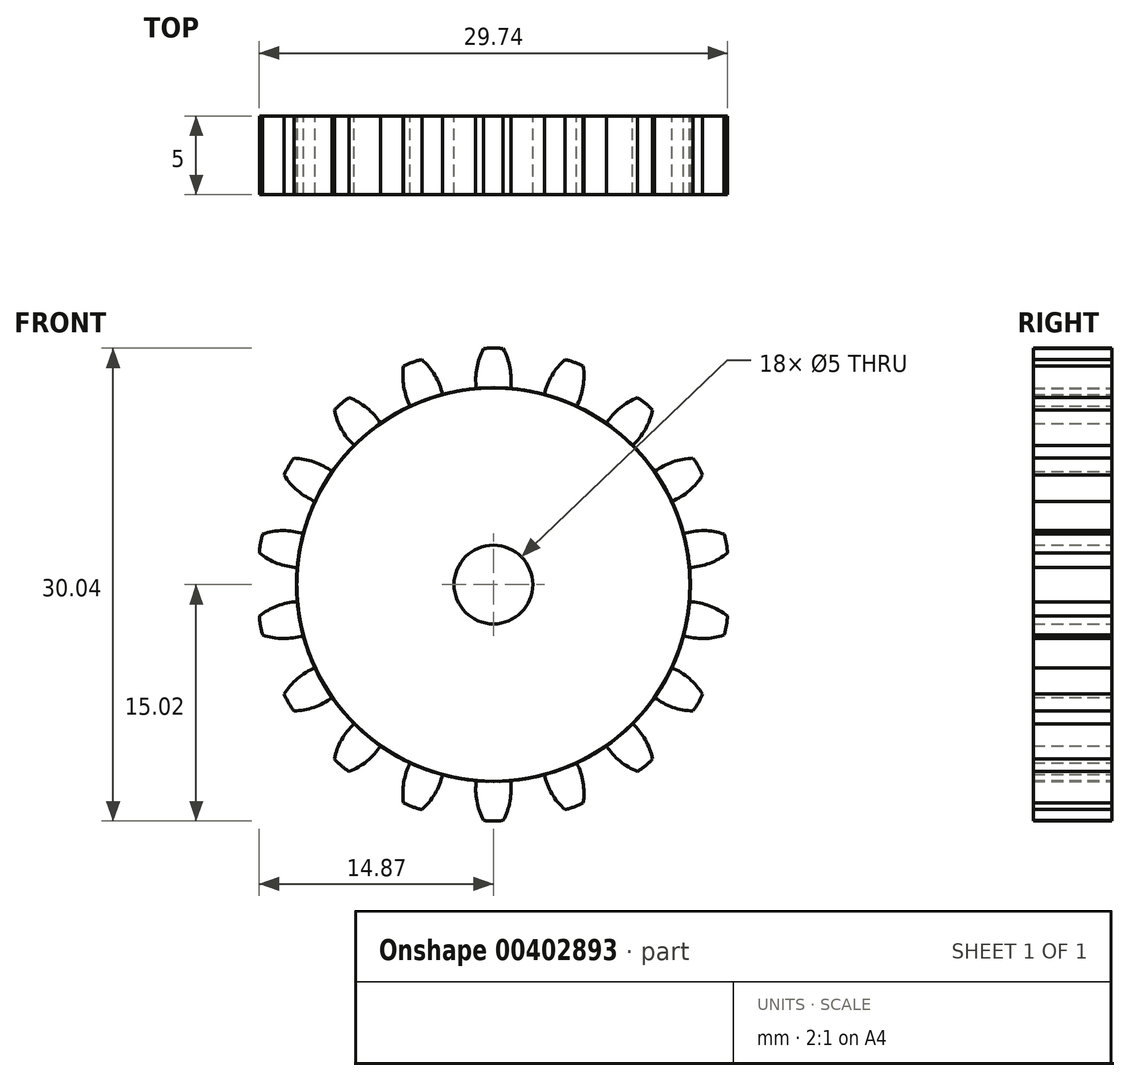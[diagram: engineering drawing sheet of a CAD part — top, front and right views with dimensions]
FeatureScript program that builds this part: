
annotation { "Feature Type Name" : "Feature", "Feature Type Description" : "" }
export const myFeature = defineFeature(function(context is Context, id is Id, definition is map)
    precondition{}
    {
        {
            var Q0;
            Q0=qCreatedBy(makeId("Front.planeOp"),FACE);
            var sketch = newSketch(context, id + "F0", { "sketchPlane" : qUnion([Q0])});
            skCircle(sketch, "E0", {"center": v(0, 0) * mm, "radius": 12.5 * mm});
            skArc(sketch, "E1", {"start": v(-0.61, 14.99) * mm, "mid": v(-1.05, 13.76) * mm, "end": v(-1.09, 12.45) * mm});
            skArc(sketch, "E2.MirrorCS", {"start": v(0.61, 14.99) * mm, "mid": v(1.05, 13.76) * mm, "end": v(1.09, 12.45) * mm});
            skArc(sketch, "E3", {"start": v(0.61, 14.99) * mm, "mid": v(0, 15.02) * mm, "end": v(-0.61, 14.99) * mm});
            skCircle(sketch, "E4", {"center": v(0, 0) * mm, "radius": 2.5 * mm});
            skSolve(sketch);
        }
        {
            var Q0;
            Q0 = qSketchRegion(id + "F0", true);
            extrude(context, id + "F1", {"entities" : qUnion([Q0]), "depth" : 5 * mm});
        }
        {
            var Q0;
            Q0=makeQuery(id+"F1.opExtrude","SWEPT_BODY",BODY,{"disambiguationData":[OSD([sQuery(id+"F0.wireOp",EDGE,"E0"),sQuery(id+"F0.wireOp",EDGE,"E1"),sQuery(id+"F0.wireOp",EDGE,"E2.MirrorCS"),sQuery(id+"F0.wireOp",EDGE,"E3")])]});
            var Q1;
            Q1=makeQuery(id+"F1.opExtrude","SWEPT_FACE",FACE,{"disambiguationData":[OSD([sQuery(id+"F0.wireOp",EDGE,"E0")])]});
            circularPattern(context, id + "F2", {"entities" : qUnion([Q0]), "axis" : qUnion([Q1]), "angle" : 360 * degree, "instanceCount" : 18, "equalSpace" : true});
        }
    });
